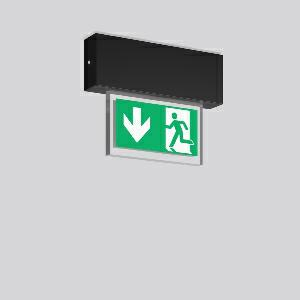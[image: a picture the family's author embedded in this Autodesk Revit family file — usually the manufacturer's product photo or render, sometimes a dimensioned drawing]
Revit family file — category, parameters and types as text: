
# Revit family: halyxx_671504_003_1_6044
name_source: partatom
category: Lighting Fixtures
units: mm (PartAtom-declared; Revit-internal decimal feet)

## family parameters
Cut with Voids When Loaded = No
Host = Face
Light Source = No
Part Type = Normal
Room Calculation Point = No
Round Connector Dimension = Use Diameter
Shared = No

## types (1)
- HALYXX (1 x LED Modul 840, 45 lm, 4000)
    Apparent Load = 2 VA
    Approval mark = CE
    CIE Flux Codes = 18 46 75 53 100
    Color Rendering = 80
    Color Temperature = 4000
    Default Elevation = 1800 mm
    Description = Series: HALYXX
Luminaire for escape route identification. Housing: extruded aluminium profile, anodised or powder-coated. Display panel: highly transparent panel, plastic, with legend on one side/both sides. Driver integrated. Suitable for connection to central battery systems. Please indicate legend number when placing your order! 
Colour: black
Length: 233 mm
Width: 40 mm
Height: 184 mm
Weight: 0.89 kg
Operating mode: maintained power mode
Viewing Distance: 14 m
Lamp: LED
Socket: without socket
Colour temperature: 4000K
Colour rendering index (CRI): 80
System power: 2 W
Rated luminous flux: 45 lm
Luminous flux, emergency: 45
System power, emergency: 1.8 W
Control gear: Regulated power supply
Protection class: I
Type of protection: IP 40
    Height = 184 mm
    Lamp = 1 x LED Modul 840
    Lamp Light Flux = 45 lm
    Lamp count = 1
    Length = 233 mm
    Lifetime = 50000 h
    Luminous efficacy = 23 lm/W
    Manufacturer = RZB
    ModVariant = No
    Model = 671504.003.1
    Mounting Place = Ceiling
    Mounting Type = Surface mounted
    Number of Poles = 1
    OnlyDefault = Yes
    Power Factor = 1
    Product Name = HALYXX
    Product group = Surface mounted ceiling luminaires
    ProductGroupID = 303
    Protection Class = Protection class I
    Protection Degree = IP 40
    RLX_Detail_Level = 1
    RLX_Emergency_Light_Flux = 45 lm
    RLX_Emergency_Type = 3
    RLX_Emergency_Type_DB = Yes
    RlxData = <blob elided: 34881 chars, md5=20a8861f>
    Socket = socket
    Standby Power = 0 W
    System Light Flux = 45 lm
    System Power = 2 W
    Type Comments = Product without accessories
    Type Image = 671502.003.jpg
    URL = http://relux.com
    VarID = ---
    Voltage = 230 V
    Voltage Range = 220-240 V
    Weight = 0.00 kg
    Width = 40 mm  [stored 0.131234 ft]

note: [stored X ft] marks values corroborated as IEEE doubles in the binary element streams (Revit-internal decimal feet)

## geometry (parser evidence)
native form markers: Blend x4, Sweep x13
no freeform markers — native parametric forms only
